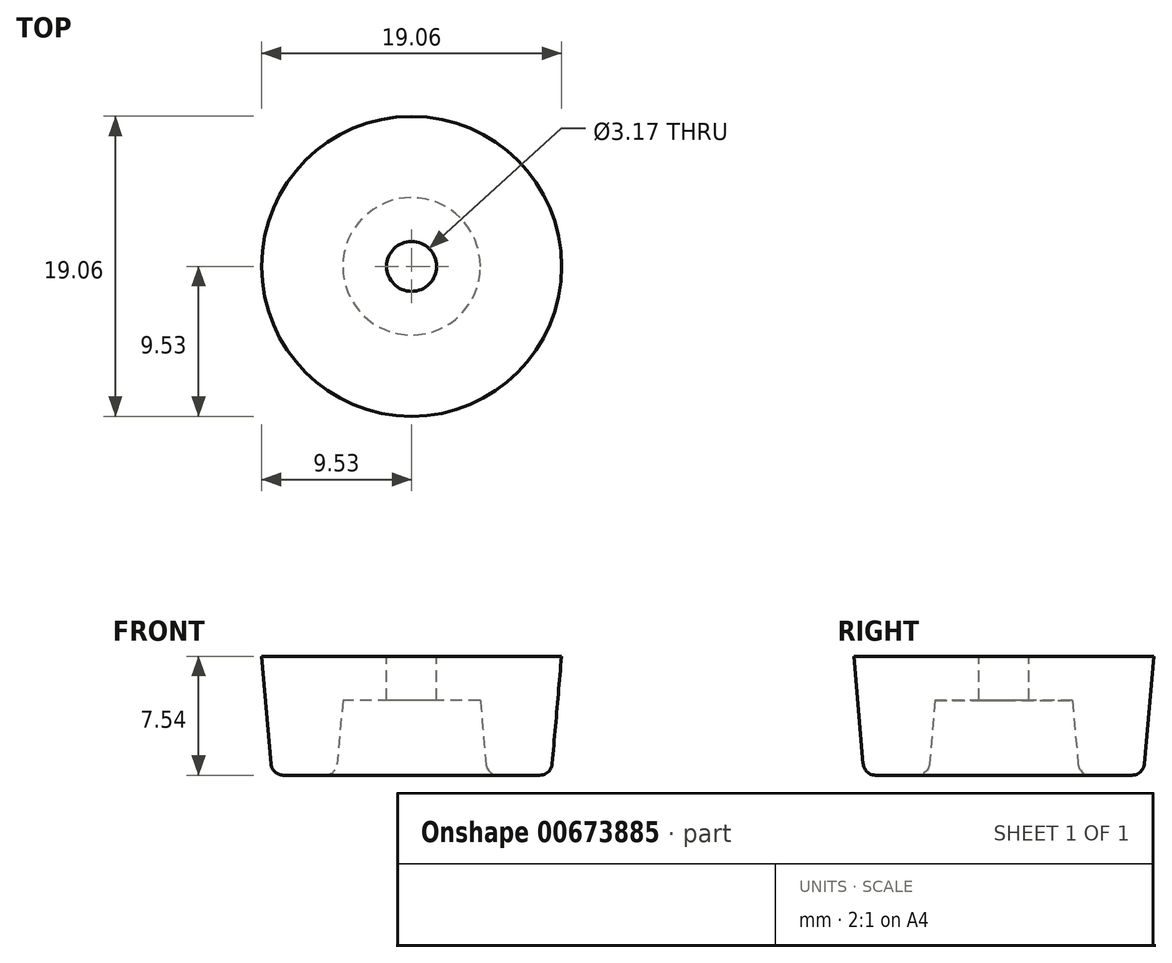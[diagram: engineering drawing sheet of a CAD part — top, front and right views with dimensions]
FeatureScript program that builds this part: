
annotation { "Feature Type Name" : "Feature", "Feature Type Description" : "" }
export const myFeature = defineFeature(function(context is Context, id is Id, definition is map)
    precondition{}
    {
        {
            var Q0;
            Q0=qCreatedBy(makeId("Front.planeOp"),FACE);
            var sketch = newSketch(context, id + "F0", { "sketchPlane" : qUnion([Q0])});
            skLineSegment(sketch, "E0", {"start": v(-9.53, 0) * mm, "end": v(-8.87, -7.54) * mm});
            skLineSegment(sketch, "E1", {"start": v(-8.87, -7.54) * mm, "end": v(-4.78, -7.54) * mm});
            skLineSegment(sketch, "E2", {"start": v(-4.78, -7.54) * mm, "end": v(-4.37, -2.78) * mm});
            skLineSegment(sketch, "E3", {"start": v(-4.37, -2.78) * mm, "end": v(-1.59, -2.78) * mm});
            skLineSegment(sketch, "E4", {"start": v(-1.59, -2.78) * mm, "end": v(-1.59, 0) * mm});
            skLineSegment(sketch, "E5", {"start": v(-1.59, 0) * mm, "end": v(-9.53, 0) * mm});
            skLineSegment(sketch, "E6", {"start": v(-6.82, -7.54) * mm, "end": v(-6.82, 0) * mm, "construction": true});
            skLineSegment(sketch, "E7", {"start": v(0, 0) * mm, "end": v(0, -16.8) * mm, "construction": true});
            skSolve(sketch);
        }
        {
            var Q0;
            Q0=makeQuery(id+"F0.imprint","IMPRINT",FACE,{"disambiguationData":[TD([[makeQuery(id+"F0.imprint","IMPRINT",EDGE,{"derivedFrom":sQuery(id+"F0.wireOp",EDGE,"E0")}),1.0]])]});
            var Q1;
            Q1=sQuery(id+"F0.wireOp",EDGE,"E0");
            var Q2;
            Q2=sQuery(id+"F0.wireOp",EDGE,"E7");
            revolve(context, id + "F1", {"entities" : qUnion([Q0]), "surfaceEntities" : qUnion([Q1]), "axis" : qUnion([Q2]), "revolveType" : RevolveType.FULL});
        }
        {
            var Q0;
            Q0=makeQuery(id+"F1.opRevolve","SWEPT_EDGE",EDGE,{"disambiguationData":[OSD([sQuery(id+"F0.wireOp",EDGE,"E0"),sQuery(id+"F0.wireOp",EDGE,"E1")])]});
            var Q1;
            Q1=makeQuery(id+"F1.opRevolve","SWEPT_EDGE",EDGE,{"disambiguationData":[OSD([sQuery(id+"F0.wireOp",EDGE,"E1"),sQuery(id+"F0.wireOp",EDGE,"E2")])]});
            fillet(context, id + "F2", {"entities" : qUnion([Q0, Q1]), "radius" : 0.8 * mm, "tangentPropagation" : true, "allowEdgeOverflow" : false});
        }
    });
